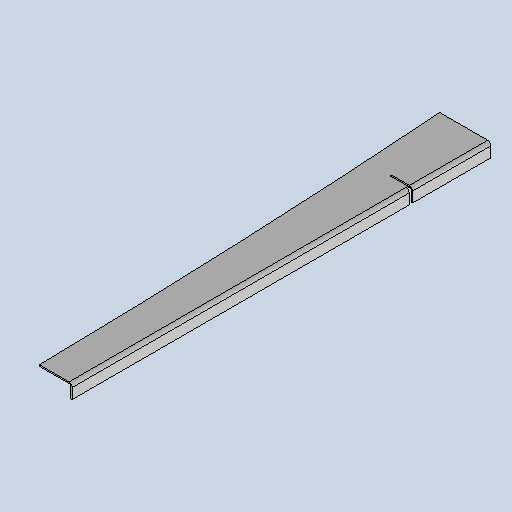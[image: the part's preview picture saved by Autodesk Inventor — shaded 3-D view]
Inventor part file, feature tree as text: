
AUTODESK INVENTOR PART (.ipt)
format: ipt  version: 2025 (Build 290162010, 162A)  size: 424,448 bytes
history: native  units: mm
features: sketch x6, other x5, sheet_metal_op x4, projected_geometry x4, extrude x2, chamfer x1, pattern_linear x1
ambient origin geometry x8: Origin, YZ Plane, XZ Plane, XY Plane, X Axis, Y Axis, Z Axis, Center Point
bodies: Body1 (feature_tree)
feature tree (23):
  sheet_metal_op  "Face2"
  sheet_metal_op  "Flange2"
  extrude  "Extrusion2"  Depth=6.0mm
  chamfer  "Chamfer2"  Distance=2.75mm
  pattern_linear  "Rectangular Pattern3"  Count1=2 Spacing1=90.0deg
  other  "Mark1"
  other  "A-Side Definition"
  extrude  "Extrusion3"  Depth=2.0mm
  sketch  "Sketch1"  dims[d16=1500.0mm d17=2700.0mm d18=2100.0mm d19=6.0mm d20=3.0mm d21=3.0mm d22=6.0mm d23=3.0mm d24=241.9mm d25=50.0mm d26=50.0mm d27=3.0mm d28=110.0mm d29=25.0mm d30=104.0mm d31=25.0mm d32=20.0mm d33=50.0mm d37=6.0mm d38=3.0mm d39=3.0mm]
  other  "Plate3"
  sketch  "Sketch3"  dims[d46=2.0mm]
  other  "Plate4"
  sheet_metal_op  "Bend2"
  sheet_metal_op  "Corner2"
  sketch  "Sketch5"  dims[d47=2.0mm]
  projected_geometry  "Projected Loop2"
  sketch  "Sketch Rectangular Pattern1"  dims[d43=3.0mm]
  sketch  "Sketch6"  dims[d48=1.0mm]
  sketch  "Sketch7"  dims[d49=4.0mm d50=2.75mm d51=20.0mm d52=90.0deg d53=2.75mm d54=8.0mm d55=2.0mm d56=2.75mm d57=500.0mm d58=500.0mm d59=500.0mm d60=500.0mm d61=500.0mm d69=1839.242466mm d70=2.0mm d71=0.0mm d72=0.0mm d76=67.563014mm d77=30.0mm d79=30.0mm d80=48.359031mm d81=30.0mm d83=250.0mm d84=40.0mm d86=550.0mm d87=10.0mm d89=10.0mm d91=274.556536mm d94=5.0mm d95=30.0mm d96=5.0mm d97=30.0mm d98=5.0mm d102=77.905549mm d104=51.799453mm d106=2.0mm d107=5.0mm d108=116.0mm d109=500.0mm d110=500.0mm d111=500.0mm d112=31.0mm d113=40.0mm d115=500.0mm d117=8.0mm d118=2.0mm d119=45.0deg d120=200.0mm d121=14.0mm d124=50.0mm d125=12.0mm d126=50.0mm d127=25.0mm d128=50.0mm d129=12.0mm d130=50.0mm d131=12.0mm d132=50.0mm d133=12.0mm d134=50.0mm d135=25.0mm d136=25.0mm d137=25.0mm d138=50.0mm d139=50.0mm d140=50.0mm d141=0.0mm d142=0.0mm d143=80.0mm]
  projected_geometry  "Projected Loop3"
  projected_geometry  "Projected Loop4"
  projected_geometry  "Projected Loop5"
  other  "Definition1"
